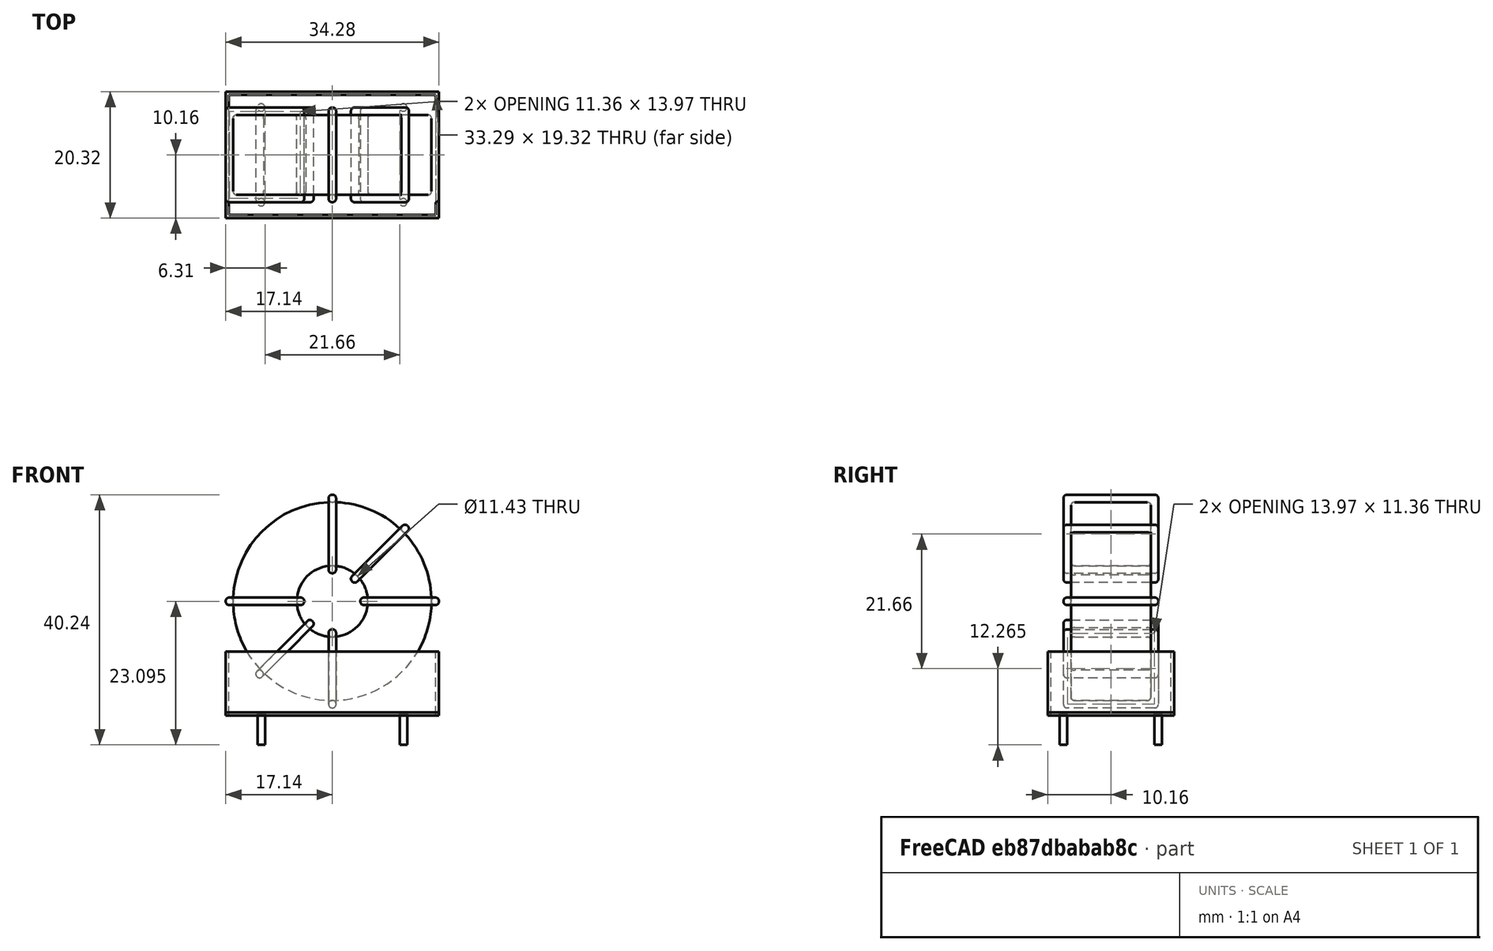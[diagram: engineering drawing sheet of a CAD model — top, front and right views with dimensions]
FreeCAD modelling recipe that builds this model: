
FCSTD DOCUMENT  (FreeCAD 0.16R6703 (Git))
Label: L_CommonModeChoke_Toroid_Vertical_L34.3mm_W20.3mm_Px15.24mm_Py22.86mm_Bourns_8100series
License: All rights reserved
LicenseURL: http://en.wikipedia.org/wiki/All_rights_reserved
objects: Sketcher::SketchObject×8, PartDesign::Pad×8, PartDesign::Fillet×5, Spreadsheet::Sheet×1
note: 29 computed .brp shape members not serialized (recipe doc carries the construction recipe); baked Part::Feature solids carry a one-line shape summary decoded from their .brp

FEATURE [Spreadsheet::Sheet] Spreadsheet  label="dimensions"
  cells = A1=Wx; B1(Wx)=34.29; C1(WW)=11.43; D1(iWx)=34.29; A2=Wy; B2(Wy)=15.24; D2(iWy)=20.32; A3=RM; B3(RMx)=15.24; C3(RMy)=22.86; A4=d_wire; B4(d_wire)=1.2; A5=H; B5(H)=31; A6=offsetx; B6(offsetx)=5.715
FEATURE [Sketcher::SketchObject] Sketch
  Placement = pos=(11.43,-7.62,0) rot=(1,0,0;1.5708rad)
  expr: Placement.Base.x = Spreadsheet.RMy / 2
  expr: Constraints[4] = Spreadsheet.WW / 2
  expr: Placement.Base.y = -Spreadsheet.RMx / 2
  expr: Constraints[0] = Spreadsheet.Wx / 2 - Spreadsheet.d_wire
  expr: Constraints[2] = Spreadsheet.Wx / 2 + Spreadsheet.d_wire + 0.5
  sketch-geometry (2):
    g0: Circle CenterX=0 CenterY=18.845 CenterZ=0 NormalX=0 NormalY=0 NormalZ=1 Radius=15.945
    g1: Circle CenterX=0 CenterY=18.845 CenterZ=0 NormalX=0 NormalY=0 NormalZ=1 Radius=5.715
  constraints (5):
    c: Radius(g0) = 15.945
    c: DistanceX(g-1,g0) = 0
    c: DistanceY(g-1,g0) = 18.845
    c: Coincident(g1,g0)
    c: Radius(g1) = 5.715
FEATURE [PartDesign::Pad] Pad
  Length = 12.84
  Length2 = 100
  Midplane = true
  Placement = pos=(11.43,-7.62,0) rot=(1,0,0;1.5708rad)
  Sketch = -> Sketch
  Type = 0
  expr: Length = Spreadsheet.Wy - 2 * Spreadsheet.d_wire
FEATURE [Sketcher::SketchObject] Sketch001
  Placement = pos=(0,0,0.75) rot=(0,0,1;0rad)
  expr: Constraints[4] = Spreadsheet.RMy
  expr: Constraints[2] = -Spreadsheet.RMx
  expr: Constraints[1] = Spreadsheet.d_wire / 2
  sketch-geometry (4):
    g0: Circle CenterX=0 CenterY=0 CenterZ=0 NormalX=0 NormalY=0 NormalZ=1 Radius=0.6
    g1: Circle CenterX=22.86 CenterY=-15.24 CenterZ=0 NormalX=0 NormalY=0 NormalZ=1 Radius=0.6
    g2: Circle CenterX=0 CenterY=-15.24 CenterZ=0 NormalX=0 NormalY=0 NormalZ=1 Radius=0.6
    g3: Circle CenterX=22.86 CenterY=0 CenterZ=0 NormalX=0 NormalY=0 NormalZ=1 Radius=0.6
  constraints (11):
    c: Equal(g0,g1)
    c: Radius(g0) = 0.6
    c: DistanceY(g-1,g1) = -15.24
    c: Coincident(g0,g-1)
    c: DistanceX(g-1,g1) = 22.86
    c: PointOnObject(g2,g-2)
    c: DistanceY(g-1,g3) = 0
    c: DistanceY(g2,g1) = 0
    c: DistanceX(g3,g1) = 0
    c: Equal(g3,g2)
    c: Equal(g2,g1)
FEATURE [PartDesign::Pad] Pad001
  Length = 5
  Length2 = 0
  Placement = pos=(0,0,0.75) rot=(0,0,1;0rad)
  Reversed = true
  Sketch = -> Sketch001
  Type = 0
FEATURE [PartDesign::Fillet] Fillet
  Base = -> Pad [Edge6,Edge3,Edge2]
  Placement = pos=(11.43,-7.62,0) rot=(1,0,0;1.5708rad)
  Radius = 0.5
FEATURE [Sketcher::SketchObject] Sketch003
  Placement = pos=(11.43,0,18.845) rot=(1,0,0;3.14159rad)
  expr: Placement.Base.x = Spreadsheet.RMy / 2
  expr: Constraints[18] = Spreadsheet.d_wire
  expr: Constraints[16] = Spreadsheet.d_wire
  expr: Constraints[19] = Spreadsheet.d_wire
  expr: Constraints[17] = Spreadsheet.d_wire
  expr: Placement.Base.y = -1 * (Spreadsheet.RMx - Spreadsheet.Wy) / 2
  expr: Constraints[21] = (Spreadsheet.Wx - Spreadsheet.WW) / 2 - Spreadsheet.d_wire
  expr: Constraints[22] = Spreadsheet.Wx / 2 - Spreadsheet.d_wire
  expr: Constraints[43] = Spreadsheet.d_wire
  expr: Constraints[48] = Spreadsheet.Wx - Spreadsheet.d_wire * 2
  expr: Constraints[49] = Spreadsheet.Wy
  expr: Placement.Base.z = Spreadsheet.Wx / 2 + Spreadsheet.d_wire + 0.5
  sketch-geometry (16):
    g0: LineSegment StartX=-4.515 StartY=0 StartZ=0 EndX=-17.145 EndY=0 EndZ=0
    g1: LineSegment StartX=-17.145 StartY=0 StartZ=0 EndX=-17.145 EndY=15.24 EndZ=0
    g2: LineSegment StartX=-17.145 StartY=15.24 StartZ=0 EndX=-4.515 EndY=15.24 EndZ=0
    g3: LineSegment StartX=-4.515 StartY=15.24 StartZ=0 EndX=-4.515 EndY=0 EndZ=0
    g4: LineSegment StartX=-15.945 StartY=14.04 StartZ=0 EndX=-5.715 EndY=14.04 EndZ=0
    g5: LineSegment StartX=-5.715 StartY=14.04 StartZ=0 EndX=-5.715 EndY=1.2 EndZ=0
    g6: LineSegment StartX=-5.715 StartY=1.2 StartZ=0 EndX=-15.945 EndY=1.2 EndZ=0
    g7: LineSegment StartX=-15.945 StartY=1.2 StartZ=0 EndX=-15.945 EndY=14.04 EndZ=0
    g8: LineSegment StartX=4.515 StartY=15.24 StartZ=0 EndX=17.145 EndY=15.24 EndZ=0
    g9: LineSegment StartX=17.145 StartY=15.24 StartZ=0 EndX=17.145 EndY=0 EndZ=0
    g10: LineSegment StartX=17.145 StartY=0 StartZ=0 EndX=4.515 EndY=0 EndZ=0
    g11: LineSegment StartX=4.515 StartY=0 StartZ=0 EndX=4.515 EndY=15.24 EndZ=0
    g12: LineSegment StartX=5.715 StartY=14.04 StartZ=0 EndX=15.945 EndY=14.04 EndZ=0
    g13: LineSegment StartX=15.945 StartY=14.04 StartZ=0 EndX=15.945 EndY=1.2 EndZ=0
    g14: LineSegment StartX=15.945 StartY=1.2 StartZ=0 EndX=5.715 EndY=1.2 EndZ=0
    g15: LineSegment StartX=5.715 StartY=1.2 StartZ=0 EndX=5.715 EndY=14.04 EndZ=0
  constraints (50):
    c: Horizontal(g0)
    c: Coincident(g1,g0)
    c: Vertical(g1)
    c: Coincident(g2,g1)
    c: Horizontal(g2)
    c: Coincident(g3,g2)
    c: Coincident(g3,g0)
    c: Vertical(g3)
    c: Coincident(g4,g5)
    c: Coincident(g5,g6)
    c: Coincident(g6,g7)
    c: Coincident(g7,g4)
    c: Horizontal(g4)
    c: Horizontal(g6)
    c: Vertical(g5)
    c: Vertical(g7)
    c: DistanceX(g1,g4) = 1.2
    c: DistanceY(g4,g1) = 1.2
    c: DistanceX(g5,g0) = 1.2
    c: DistanceY(g0,g5) = 1.2
    c: DistanceY(g-1,g0) = 0
    c: DistanceX(g6,g6) = 10.23
    c: DistanceX(g6,g-1) = 15.945
    c: Coincident(g8,g9)
    c: Coincident(g9,g10)
    c: Coincident(g10,g11)
    c: Coincident(g11,g8)
    c: Horizontal(g8)
    c: Horizontal(g10)
    c: Vertical(g9)
    c: Vertical(g11)
    c: Coincident(g12,g13)
    c: Coincident(g13,g14)
    c: Coincident(g14,g15)
    c: Coincident(g15,g12)
    c: Horizontal(g12)
    c: Horizontal(g14)
    c: Vertical(g13)
    c: Vertical(g15)
    c: DistanceY(g8,g2) = 0
    c: DistanceY(g10,g0) = 0
    c: DistanceY(g14,g5) = 0
    c: DistanceY(g12,g4) = 0
    c: DistanceX(g8,g12) = 1.2
    c: Equal(g8,g2)
    c: Equal(g12,g4)
    c: Equal(g9,g1)
    c: Equal(g13,g7)
    c: DistanceX(g4,g12) = 31.89
    c: DistanceY(g0,g1) = 15.24
FEATURE [PartDesign::Pad] Pad002
  Length = 1.2
  Length2 = 100
  Midplane = true
  Placement = pos=(11.43,0,18.845) rot=(1,0,0;3.14159rad)
  Sketch = -> Sketch003
  Type = 0
  expr: Length = Spreadsheet.d_wire
FEATURE [PartDesign::Fillet] Fillet001
  Base = -> Pad002 [Edge38,Edge41,Edge42,Edge43,Edge29,Edge32,Edge33,Edge34,Edge25,Edge35,Edge36,Edge13,Edge14,Edge15,Edge16,Edge17,Edge18,Edge19,Edge1,Edge2,Edge3,Edge4,Edge5,Edge6,Edge7,Edge37,Edge39,Edge40,Edge20,Edge23,Edge24,Edge21,Edge22,Edge8,Edge9,Edge10,Edge11,Edge12,Edge26,Edge27,+8 more]
  Placement = pos=(11.43,0,18.845) rot=(1,0,0;3.14159rad)
  Radius = 0.564
  expr: Radius = Spreadsheet.d_wire * 0.47
FEATURE [Sketcher::SketchObject] Sketch004
  Placement = pos=(11.43,0,18.845) rot=(0.92388,0,0.382683;3.14159rad)
  expr: Placement.Base.x = Spreadsheet.RMy / 2
  expr: Constraints[18] = Spreadsheet.d_wire
  expr: Constraints[16] = Spreadsheet.d_wire
  expr: Constraints[19] = Spreadsheet.d_wire
  expr: Constraints[17] = Spreadsheet.d_wire
  expr: Placement.Base.y = -1 * (Spreadsheet.RMx - Spreadsheet.Wy) / 2
  expr: Constraints[21] = (Spreadsheet.Wx - Spreadsheet.WW) / 2 - Spreadsheet.d_wire
  expr: Constraints[22] = Spreadsheet.Wx / 2 - Spreadsheet.d_wire
  expr: Constraints[43] = Spreadsheet.d_wire
  expr: Constraints[48] = Spreadsheet.Wx - 2 * Spreadsheet.d_wire
  expr: Constraints[49] = Spreadsheet.Wy
  expr: Placement.Base.z = Spreadsheet.Wx / 2 + Spreadsheet.d_wire + 0.5
  sketch-geometry (16):
    g0: LineSegment StartX=-4.515 StartY=0 StartZ=0 EndX=-17.145 EndY=0 EndZ=0
    g1: LineSegment StartX=-17.145 StartY=0 StartZ=0 EndX=-17.145 EndY=15.24 EndZ=0
    g2: LineSegment StartX=-17.145 StartY=15.24 StartZ=0 EndX=-4.515 EndY=15.24 EndZ=0
    g3: LineSegment StartX=-4.515 StartY=15.24 StartZ=0 EndX=-4.515 EndY=0 EndZ=0
    g4: LineSegment StartX=-15.945 StartY=14.04 StartZ=0 EndX=-5.715 EndY=14.04 EndZ=0
    g5: LineSegment StartX=-5.715 StartY=14.04 StartZ=0 EndX=-5.715 EndY=1.2 EndZ=0
    g6: LineSegment StartX=-5.715 StartY=1.2 StartZ=0 EndX=-15.945 EndY=1.2 EndZ=0
    g7: LineSegment StartX=-15.945 StartY=1.2 StartZ=0 EndX=-15.945 EndY=14.04 EndZ=0
    g8: LineSegment StartX=4.515 StartY=15.24 StartZ=0 EndX=17.145 EndY=15.24 EndZ=0
    g9: LineSegment StartX=17.145 StartY=15.24 StartZ=0 EndX=17.145 EndY=0 EndZ=0
    g10: LineSegment StartX=17.145 StartY=0 StartZ=0 EndX=4.515 EndY=0 EndZ=0
    g11: LineSegment StartX=4.515 StartY=0 StartZ=0 EndX=4.515 EndY=15.24 EndZ=0
    g12: LineSegment StartX=5.715 StartY=14.04 StartZ=0 EndX=15.945 EndY=14.04 EndZ=0
    g13: LineSegment StartX=15.945 StartY=14.04 StartZ=0 EndX=15.945 EndY=1.2 EndZ=0
    g14: LineSegment StartX=15.945 StartY=1.2 StartZ=0 EndX=5.715 EndY=1.2 EndZ=0
    g15: LineSegment StartX=5.715 StartY=1.2 StartZ=0 EndX=5.715 EndY=14.04 EndZ=0
  constraints (50):
    c: Horizontal(g0)
    c: Coincident(g1,g0)
    c: Vertical(g1)
    c: Coincident(g2,g1)
    c: Horizontal(g2)
    c: Coincident(g3,g2)
    c: Coincident(g3,g0)
    c: Vertical(g3)
    c: Coincident(g4,g5)
    c: Coincident(g5,g6)
    c: Coincident(g6,g7)
    c: Coincident(g7,g4)
    c: Horizontal(g4)
    c: Horizontal(g6)
    c: Vertical(g5)
    c: Vertical(g7)
    c: DistanceX(g1,g4) = 1.2
    c: DistanceY(g4,g1) = 1.2
    c: DistanceX(g5,g0) = 1.2
    c: DistanceY(g0,g5) = 1.2
    c: DistanceY(g-1,g0) = 0
    c: DistanceX(g6,g6) = 10.23
    c: DistanceX(g6,g-1) = 15.945
    c: Coincident(g8,g9)
    c: Coincident(g9,g10)
    c: Coincident(g10,g11)
    c: Coincident(g11,g8)
    c: Horizontal(g8)
    c: Horizontal(g10)
    c: Vertical(g9)
    c: Vertical(g11)
    c: Coincident(g12,g13)
    c: Coincident(g13,g14)
    c: Coincident(g14,g15)
    c: Coincident(g15,g12)
    c: Horizontal(g12)
    c: Horizontal(g14)
    c: Vertical(g13)
    c: Vertical(g15)
    c: DistanceY(g8,g2) = 0
    c: DistanceY(g10,g0) = 0
    c: DistanceY(g14,g5) = 0
    c: DistanceY(g12,g4) = 0
    c: DistanceX(g8,g12) = 1.2
    c: Equal(g8,g2)
    c: Equal(g12,g4)
    c: Equal(g9,g1)
    c: Equal(g13,g7)
    c: DistanceX(g4,g12) = 31.89
    c: DistanceY(g0,g1) = 15.24
FEATURE [PartDesign::Pad] Pad003
  Length = 1.2
  Length2 = 100
  Midplane = true
  Placement = pos=(11.43,0,18.845) rot=(0.92388,0,0.382683;3.14159rad)
  Sketch = -> Sketch004
  Type = 0
  expr: Length = Spreadsheet.d_wire
FEATURE [PartDesign::Fillet] Fillet002
  Base = -> Pad003 [Edge38,Edge41,Edge42,Edge43,Edge29,Edge32,Edge33,Edge34,Edge25,Edge35,Edge36,Edge13,Edge14,Edge15,Edge16,Edge17,Edge18,Edge19,Edge1,Edge2,Edge3,Edge4,Edge5,Edge6,Edge7,Edge37,Edge39,Edge40,Edge20,Edge23,Edge24,Edge21,Edge22,Edge8,Edge9,Edge10,Edge11,Edge12,Edge26,Edge27,+8 more]
  Placement = pos=(11.43,0,18.845) rot=(0.92388,0,0.382683;3.14159rad)
  Radius = 0.564
  expr: Radius = Spreadsheet.d_wire * 0.47
FEATURE [Sketcher::SketchObject] Sketch005
  Placement = pos=(11.43,0,18.845) rot=(0.92388,0,-0.382683;3.14159rad)
  expr: Placement.Base.x = Spreadsheet.RMy / 2
  expr: Constraints[18] = Spreadsheet.d_wire
  expr: Constraints[16] = Spreadsheet.d_wire
  expr: Constraints[19] = Spreadsheet.d_wire
  expr: Constraints[17] = Spreadsheet.d_wire
  expr: Placement.Base.y = -1 * (Spreadsheet.RMx - Spreadsheet.Wy) / 2
  expr: Constraints[21] = (Spreadsheet.Wx - Spreadsheet.WW) / 2 - Spreadsheet.d_wire
  expr: Constraints[22] = Spreadsheet.Wx / 2 - Spreadsheet.d_wire
  expr: Constraints[43] = Spreadsheet.d_wire
  expr: Constraints[48] = Spreadsheet.Wx - 2 * Spreadsheet.d_wire
  expr: Constraints[49] = Spreadsheet.Wy
  expr: Placement.Base.z = Spreadsheet.Wx / 2 + Spreadsheet.d_wire + 0.5
  sketch-geometry (16):
    g0: LineSegment StartX=-4.515 StartY=0 StartZ=0 EndX=-17.145 EndY=0 EndZ=0
    g1: LineSegment StartX=-17.145 StartY=0 StartZ=0 EndX=-17.145 EndY=15.24 EndZ=0
    g2: LineSegment StartX=-17.145 StartY=15.24 StartZ=0 EndX=-4.515 EndY=15.24 EndZ=0
    g3: LineSegment StartX=-4.515 StartY=15.24 StartZ=0 EndX=-4.515 EndY=0 EndZ=0
    g4: LineSegment StartX=-15.945 StartY=14.04 StartZ=0 EndX=-5.715 EndY=14.04 EndZ=0
    g5: LineSegment StartX=-5.715 StartY=14.04 StartZ=0 EndX=-5.715 EndY=1.2 EndZ=0
    g6: LineSegment StartX=-5.715 StartY=1.2 StartZ=0 EndX=-15.945 EndY=1.2 EndZ=0
    g7: LineSegment StartX=-15.945 StartY=1.2 StartZ=0 EndX=-15.945 EndY=14.04 EndZ=0
    g8: LineSegment StartX=4.515 StartY=15.24 StartZ=0 EndX=17.145 EndY=15.24 EndZ=0
    g9: LineSegment StartX=17.145 StartY=15.24 StartZ=0 EndX=17.145 EndY=0 EndZ=0
    g10: LineSegment StartX=17.145 StartY=0 StartZ=0 EndX=4.515 EndY=0 EndZ=0
    g11: LineSegment StartX=4.515 StartY=0 StartZ=0 EndX=4.515 EndY=15.24 EndZ=0
    g12: LineSegment StartX=5.715 StartY=14.04 StartZ=0 EndX=15.945 EndY=14.04 EndZ=0
    g13: LineSegment StartX=15.945 StartY=14.04 StartZ=0 EndX=15.945 EndY=1.2 EndZ=0
    g14: LineSegment StartX=15.945 StartY=1.2 StartZ=0 EndX=5.715 EndY=1.2 EndZ=0
    g15: LineSegment StartX=5.715 StartY=1.2 StartZ=0 EndX=5.715 EndY=14.04 EndZ=0
  constraints (50):
    c: Horizontal(g0)
    c: Coincident(g1,g0)
    c: Vertical(g1)
    c: Coincident(g2,g1)
    c: Horizontal(g2)
    c: Coincident(g3,g2)
    c: Coincident(g3,g0)
    c: Vertical(g3)
    c: Coincident(g4,g5)
    c: Coincident(g5,g6)
    c: Coincident(g6,g7)
    c: Coincident(g7,g4)
    c: Horizontal(g4)
    c: Horizontal(g6)
    c: Vertical(g5)
    c: Vertical(g7)
    c: DistanceX(g1,g4) = 1.2
    c: DistanceY(g4,g1) = 1.2
    c: DistanceX(g5,g0) = 1.2
    c: DistanceY(g0,g5) = 1.2
    c: DistanceY(g-1,g0) = 0
    c: DistanceX(g6,g6) = 10.23
    c: DistanceX(g6,g-1) = 15.945
    c: Coincident(g8,g9)
    c: Coincident(g9,g10)
    c: Coincident(g10,g11)
    c: Coincident(g11,g8)
    c: Horizontal(g8)
    c: Horizontal(g10)
    c: Vertical(g9)
    c: Vertical(g11)
    c: Coincident(g12,g13)
    c: Coincident(g13,g14)
    c: Coincident(g14,g15)
    c: Coincident(g15,g12)
    c: Horizontal(g12)
    c: Horizontal(g14)
    c: Vertical(g13)
    c: Vertical(g15)
    c: DistanceY(g8,g2) = 0
    c: DistanceY(g10,g0) = 0
    c: DistanceY(g14,g5) = 0
    c: DistanceY(g12,g4) = 0
    c: DistanceX(g8,g12) = 1.2
    c: Equal(g8,g2)
    c: Equal(g12,g4)
    c: Equal(g9,g1)
    c: Equal(g13,g7)
    c: DistanceX(g4,g12) = 31.89
    c: DistanceY(g0,g1) = 15.24
FEATURE [PartDesign::Pad] Pad004
  Length = 1.2
  Length2 = 100
  Midplane = true
  Placement = pos=(11.43,0,18.845) rot=(0.92388,0,-0.382683;3.14159rad)
  Sketch = -> Sketch005
  Type = 0
  expr: Length = Spreadsheet.d_wire
FEATURE [PartDesign::Fillet] Fillet003
  Base = -> Pad004 [Edge38,Edge41,Edge42,Edge43,Edge29,Edge32,Edge33,Edge34,Edge25,Edge35,Edge36,Edge13,Edge14,Edge15,Edge16,Edge17,Edge18,Edge19,Edge1,Edge2,Edge3,Edge4,Edge5,Edge6,Edge7,Edge37,Edge39,Edge40,Edge20,Edge23,Edge24,Edge21,Edge22,Edge8,Edge9,Edge10,Edge11,Edge12,Edge26,Edge27,+8 more]
  Placement = pos=(11.43,0,18.845) rot=(0.92388,0,-0.382683;3.14159rad)
  Radius = 0.564
  expr: Radius = Spreadsheet.d_wire * 0.47
FEATURE [Sketcher::SketchObject] Sketch006
  Placement = pos=(11.43,0,18.845) rot=(0.707107,0,0.707107;3.14159rad)
  expr: Placement.Base.x = Spreadsheet.RMy / 2
  expr: Constraints[18] = Spreadsheet.d_wire
  expr: Constraints[16] = Spreadsheet.d_wire
  expr: Constraints[19] = Spreadsheet.d_wire
  expr: Constraints[17] = Spreadsheet.d_wire
  expr: Placement.Base.y = -1 * (Spreadsheet.RMx - Spreadsheet.Wy) / 2
  expr: Constraints[21] = (Spreadsheet.Wx - Spreadsheet.WW) / 2 - Spreadsheet.d_wire
  expr: Constraints[22] = Spreadsheet.Wx / 2 - Spreadsheet.d_wire
  expr: Constraints[43] = Spreadsheet.d_wire
  expr: Constraints[48] = Spreadsheet.Wx - Spreadsheet.d_wire * 2
  expr: Constraints[49] = Spreadsheet.Wy
  expr: Placement.Base.z = Spreadsheet.Wx / 2 + Spreadsheet.d_wire + 0.5
  sketch-geometry (16):
    g0: LineSegment StartX=-4.515 StartY=0 StartZ=0 EndX=-17.145 EndY=0 EndZ=0
    g1: LineSegment StartX=-17.145 StartY=0 StartZ=0 EndX=-17.145 EndY=15.24 EndZ=0
    g2: LineSegment StartX=-17.145 StartY=15.24 StartZ=0 EndX=-4.515 EndY=15.24 EndZ=0
    g3: LineSegment StartX=-4.515 StartY=15.24 StartZ=0 EndX=-4.515 EndY=0 EndZ=0
    g4: LineSegment StartX=-15.945 StartY=14.04 StartZ=0 EndX=-5.715 EndY=14.04 EndZ=0
    g5: LineSegment StartX=-5.715 StartY=14.04 StartZ=0 EndX=-5.715 EndY=1.2 EndZ=0
    g6: LineSegment StartX=-5.715 StartY=1.2 StartZ=0 EndX=-15.945 EndY=1.2 EndZ=0
    g7: LineSegment StartX=-15.945 StartY=1.2 StartZ=0 EndX=-15.945 EndY=14.04 EndZ=0
    g8: LineSegment StartX=4.515 StartY=15.24 StartZ=0 EndX=17.145 EndY=15.24 EndZ=0
    g9: LineSegment StartX=17.145 StartY=15.24 StartZ=0 EndX=17.145 EndY=0 EndZ=0
    g10: LineSegment StartX=17.145 StartY=0 StartZ=0 EndX=4.515 EndY=0 EndZ=0
    g11: LineSegment StartX=4.515 StartY=0 StartZ=0 EndX=4.515 EndY=15.24 EndZ=0
    g12: LineSegment StartX=5.715 StartY=14.04 StartZ=0 EndX=15.945 EndY=14.04 EndZ=0
    g13: LineSegment StartX=15.945 StartY=14.04 StartZ=0 EndX=15.945 EndY=1.2 EndZ=0
    g14: LineSegment StartX=15.945 StartY=1.2 StartZ=0 EndX=5.715 EndY=1.2 EndZ=0
    g15: LineSegment StartX=5.715 StartY=1.2 StartZ=0 EndX=5.715 EndY=14.04 EndZ=0
  constraints (50):
    c: Horizontal(g0)
    c: Coincident(g1,g0)
    c: Vertical(g1)
    c: Coincident(g2,g1)
    c: Horizontal(g2)
    c: Coincident(g3,g2)
    c: Coincident(g3,g0)
    c: Vertical(g3)
    c: Coincident(g4,g5)
    c: Coincident(g5,g6)
    c: Coincident(g6,g7)
    c: Coincident(g7,g4)
    c: Horizontal(g4)
    c: Horizontal(g6)
    c: Vertical(g5)
    c: Vertical(g7)
    c: DistanceX(g1,g4) = 1.2
    c: DistanceY(g4,g1) = 1.2
    c: DistanceX(g5,g0) = 1.2
    c: DistanceY(g0,g5) = 1.2
    c: DistanceY(g-1,g0) = 0
    c: DistanceX(g6,g6) = 10.23
    c: DistanceX(g6,g-1) = 15.945
    c: Coincident(g8,g9)
    c: Coincident(g9,g10)
    c: Coincident(g10,g11)
    c: Coincident(g11,g8)
    c: Horizontal(g8)
    c: Horizontal(g10)
    c: Vertical(g9)
    c: Vertical(g11)
    c: Coincident(g12,g13)
    c: Coincident(g13,g14)
    c: Coincident(g14,g15)
    c: Coincident(g15,g12)
    c: Horizontal(g12)
    c: Horizontal(g14)
    c: Vertical(g13)
    c: Vertical(g15)
    c: DistanceY(g8,g2) = 0
    c: DistanceY(g10,g0) = 0
    c: DistanceY(g14,g5) = 0
    c: DistanceY(g12,g4) = 0
    c: DistanceX(g8,g12) = 1.2
    c: Equal(g8,g2)
    c: Equal(g12,g4)
    c: Equal(g9,g1)
    c: Equal(g13,g7)
    c: DistanceX(g4,g12) = 31.89
    c: DistanceY(g0,g1) = 15.24
FEATURE [PartDesign::Pad] Pad005
  Length = 1.2
  Length2 = 100
  Midplane = true
  Placement = pos=(11.43,0,18.845) rot=(0.707107,0,0.707107;3.14159rad)
  Sketch = -> Sketch006
  Type = 0
  expr: Length = Spreadsheet.d_wire
FEATURE [PartDesign::Fillet] Fillet004
  Base = -> Pad005 [Edge38,Edge41,Edge42,Edge43,Edge29,Edge32,Edge33,Edge34,Edge25,Edge35,Edge36,Edge13,Edge14,Edge15,Edge16,Edge17,Edge18,Edge19,Edge1,Edge2,Edge3,Edge4,Edge5,Edge6,Edge7,Edge37,Edge39,Edge40,Edge20,Edge23,Edge24,Edge21,Edge22,Edge8,Edge9,Edge10,Edge11,Edge12,Edge26,Edge27,+8 more]
  Placement = pos=(11.43,0,18.845) rot=(0.707107,0,0.707107;3.14159rad)
  Radius = 0.564
  expr: Radius = Spreadsheet.d_wire * 0.47
FEATURE [Sketcher::SketchObject] Sketch007
  Placement = pos=(11.43,0,0.5) rot=(0,0,1;0rad)
  expr: Placement.Base.x = Spreadsheet.RMy / 2
  expr: Placement.Base.z = 0.5
  expr: Constraints[11] = Spreadsheet.iWx / 2
  expr: Constraints[10] = (Spreadsheet.iWy - Spreadsheet.RMx) / 2
  expr: Constraints[9] = Spreadsheet.iWy
  expr: Constraints[8] = Spreadsheet.iWx
  sketch-geometry (4):
    g0: LineSegment StartX=-17.145 StartY=2.54 StartZ=0 EndX=17.145 EndY=2.54 EndZ=0
    g1: LineSegment StartX=17.145 StartY=2.54 StartZ=0 EndX=17.145 EndY=-17.78 EndZ=0
    g2: LineSegment StartX=17.145 StartY=-17.78 StartZ=0 EndX=-17.145 EndY=-17.78 EndZ=0
    g3: LineSegment StartX=-17.145 StartY=-17.78 StartZ=0 EndX=-17.145 EndY=2.54 EndZ=0
  constraints (12):
    c: Coincident(g0,g1)
    c: Coincident(g1,g2)
    c: Coincident(g2,g3)
    c: Coincident(g3,g0)
    c: Horizontal(g0)
    c: Horizontal(g2)
    c: Vertical(g1)
    c: Vertical(g3)
    c: DistanceX(g0,g0) = 34.29
    c: DistanceY(g3,g3) = 20.32
    c: DistanceY(g-1,g0) = 2.54
    c: DistanceX(g0,g-1) = 17.145
FEATURE [PartDesign::Pad] Pad006
  Length = 0.5
  Length2 = 100
  Placement = pos=(11.43,0,0.5) rot=(0,0,1;0rad)
  Sketch = -> Sketch007
  Type = 0
FEATURE [Sketcher::SketchObject] Sketch008
  Placement = pos=(11.43,0,0.5) rot=(0,0,1;0rad)
  expr: Placement.Base.x = Spreadsheet.RMy / 2
  expr: Constraints[8] = Spreadsheet.iWx
  expr: Constraints[9] = Spreadsheet.iWy
  expr: Constraints[10] = (Spreadsheet.iWy - Spreadsheet.RMx) / 2
  expr: Placement.Base.z = 0.5
  expr: Constraints[21] = 0.5
  expr: Constraints[11] = Spreadsheet.iWx / 2
  sketch-geometry (8):
    g0: LineSegment StartX=-17.145 StartY=2.54 StartZ=0 EndX=17.145 EndY=2.54 EndZ=0
    g1: LineSegment StartX=17.145 StartY=2.54 StartZ=0 EndX=17.145 EndY=-17.78 EndZ=0
    g2: LineSegment StartX=17.145 StartY=-17.78 StartZ=0 EndX=-17.145 EndY=-17.78 EndZ=0
    g3: LineSegment StartX=-17.145 StartY=-17.78 StartZ=0 EndX=-17.145 EndY=2.54 EndZ=0
    g4: LineSegment StartX=-16.645 StartY=2.04 StartZ=0 EndX=16.645 EndY=2.04 EndZ=0
    g5: LineSegment StartX=16.645 StartY=2.04 StartZ=0 EndX=16.645 EndY=-17.28 EndZ=0
    g6: LineSegment StartX=16.645 StartY=-17.28 StartZ=0 EndX=-16.645 EndY=-17.28 EndZ=0
    g7: LineSegment StartX=-16.645 StartY=-17.28 StartZ=0 EndX=-16.645 EndY=2.04 EndZ=0
  constraints (24):
    c: Coincident(g0,g1)
    c: Coincident(g1,g2)
    c: Coincident(g2,g3)
    c: Coincident(g3,g0)
    c: Horizontal(g0)
    c: Horizontal(g2)
    c: Vertical(g1)
    c: Vertical(g3)
    c: DistanceX(g0,g0) = 34.29
    c: DistanceY(g3,g3) = 20.32
    c: DistanceY(g-1,g0) = 2.54
    c: DistanceX(g0,g-1) = 17.145
    c: Coincident(g4,g5)
    c: Coincident(g5,g6)
    c: Coincident(g6,g7)
    c: Coincident(g7,g4)
    c: Horizontal(g4)
    c: Horizontal(g6)
    c: Vertical(g5)
    c: Vertical(g7)
    c: DistanceX(g5,g1) = 0.5
    c: DistanceY(g1,g5) = 0.5
    c: DistanceX(g0,g4) = 0.5
    c: DistanceY(g4,g0) = 0.5
FEATURE [PartDesign::Pad] Pad007
  Length = 10.287
  Length2 = 100
  Placement = pos=(11.43,0,0.5) rot=(0,0,1;0rad)
  Sketch = -> Sketch008
  Type = 0
  expr: Length = Spreadsheet.Wx * 0.3
